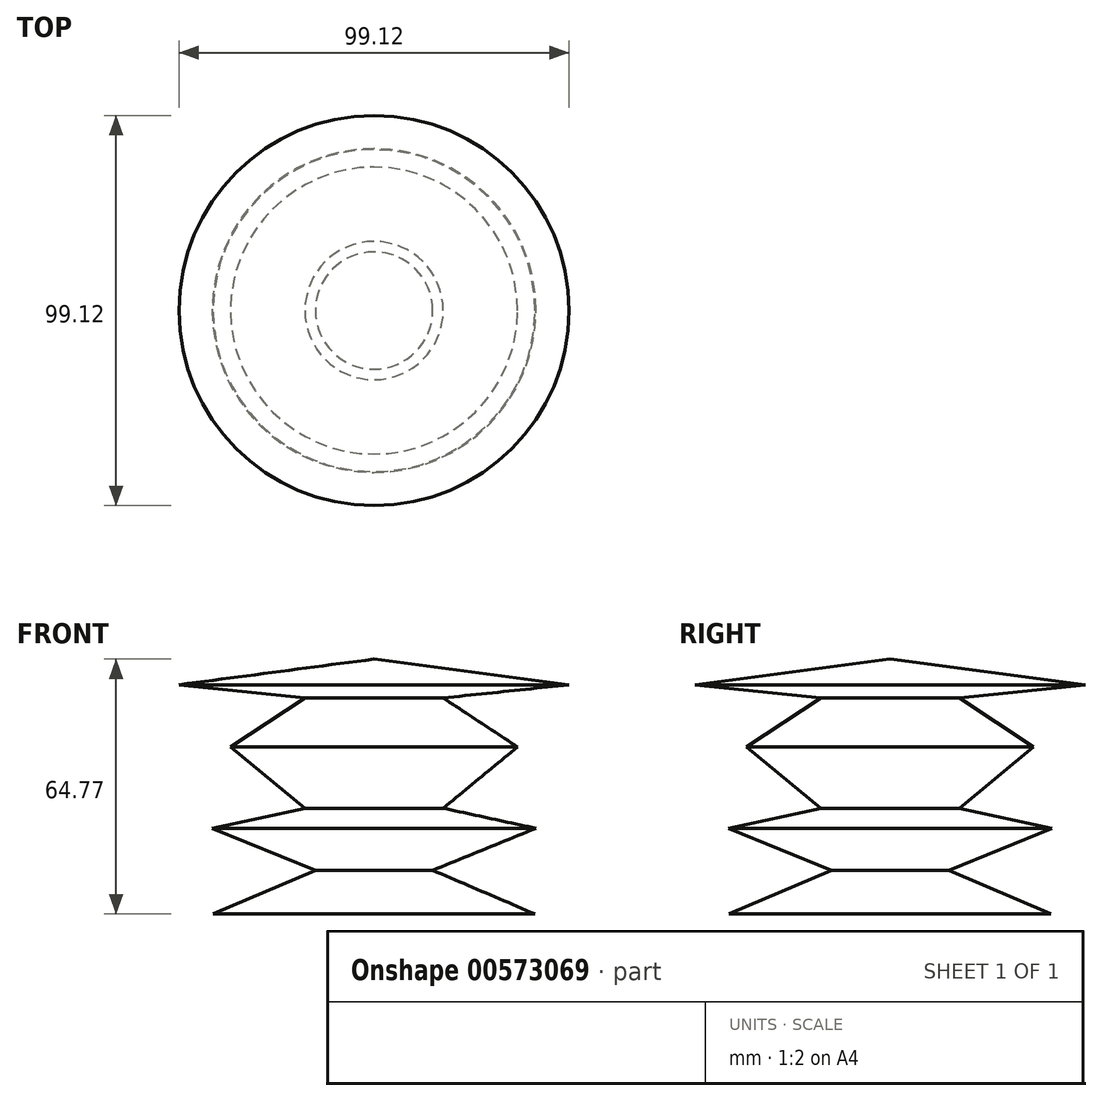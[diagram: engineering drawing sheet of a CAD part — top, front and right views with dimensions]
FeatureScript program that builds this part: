
annotation { "Feature Type Name" : "Feature", "Feature Type Description" : "" }
export const myFeature = defineFeature(function(context is Context, id is Id, definition is map)
    precondition{}
    {
        {
            var Q0;
            Q0=qCreatedBy(makeId("Front.planeOp"),FACE);
            var sketch = newSketch(context, id + "F0", { "sketchPlane" : qUnion([Q0])});
            skLineSegment(sketch, "E0", {"start": v(0, 0) * mm, "end": v(-40.9, 0) * mm});
            skLineSegment(sketch, "E1", {"start": v(-40.9, 0) * mm, "end": v(-14.9, 11.11) * mm});
            skLineSegment(sketch, "E2", {"start": v(-14.9, 11.11) * mm, "end": v(-41.12, 21.78) * mm});
            skLineSegment(sketch, "E3", {"start": v(-41.12, 21.78) * mm, "end": v(-17.56, 26.9) * mm});
            skLineSegment(sketch, "E4", {"start": v(-17.56, 26.9) * mm, "end": v(-36.45, 42.45) * mm});
            skLineSegment(sketch, "E5", {"start": v(-36.45, 42.45) * mm, "end": v(-17.56, 54.9) * mm});
            skLineSegment(sketch, "E6", {"start": v(-17.56, 54.9) * mm, "end": v(-49.56, 58.26) * mm});
            skLineSegment(sketch, "E7", {"start": v(-49.56, 58.26) * mm, "end": v(0, 64.77) * mm});
            skLineSegment(sketch, "E8", {"start": v(0, 64.77) * mm, "end": v(0, 0) * mm});
            skSolve(sketch);
        }
        {
            var Q0;
            Q0=makeQuery(id+"F0.imprint","IMPRINT",FACE,{"disambiguationData":[TD([[makeQuery(id+"F0.imprint","IMPRINT",EDGE,{"derivedFrom":sQuery(id+"F0.wireOp",EDGE,"E0")}),-1.0]])]});
            var Q1;
            Q1=sQuery(id+"F0.wireOp",EDGE,"E8");
            revolve(context, id + "F1", {"entities" : qUnion([Q0]), "axis" : qUnion([Q1]), "revolveType" : RevolveType.FULL});
        }
    });
